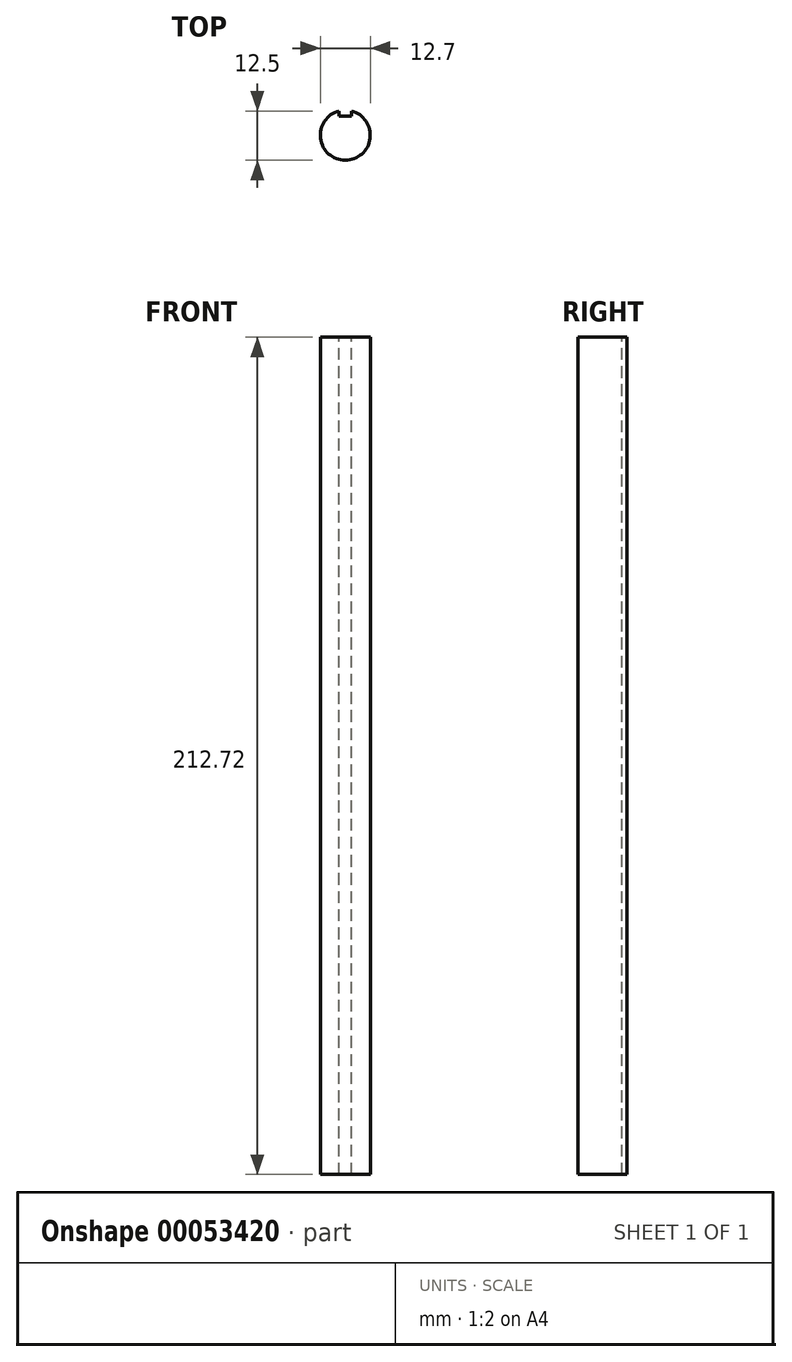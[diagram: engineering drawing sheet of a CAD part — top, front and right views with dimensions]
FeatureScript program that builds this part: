
annotation { "Feature Type Name" : "Feature", "Feature Type Description" : "" }
export const myFeature = defineFeature(function(context is Context, id is Id, definition is map)
    precondition{}
    {
        {
            var Q0;
            Q0=qCreatedBy(makeId("Top.planeOp"),FACE);
            var sketch = newSketch(context, id + "F0", { "sketchPlane" : qUnion([Q0])});
            skCircle(sketch, "E0", {"center": v(0, 0) * mm, "radius": 6.35 * mm});
            skSolve(sketch);
        }
        {
            var Q0;
            Q0=makeQuery(id+"F0.imprint","IMPRINT",FACE,{"disambiguationData":[TD([[makeQuery(id+"F0.imprint","IMPRINT",EDGE,{"derivedFrom":sQuery(id+"F0.wireOp",EDGE,"E0")}),1.0]])]});
            extrude(context, id + "F1", {"entities" : qUnion([Q0]), "depth" : 212.72 * mm});
        }
        {
            var Q0;
            Q0=makeQuery(id+"F1.opExtrude","CAP_FACE",FACE,{"disambiguationData":[OSD([sQuery(id+"F0.wireOp",EDGE,"E0")])],"isStart":false});
            var sketch = newSketch(context, id + "F2", { "sketchPlane" : qUnion([Q0])});
            skLineSegment(sketch, "E1.rect.bottom", {"start": v(1.59, 4.8) * mm, "end": v(-1.59, 4.8) * mm});
            skLineSegment(sketch, "E1.rect.top", {"start": v(1.59, 6.39) * mm, "end": v(-1.59, 6.39) * mm});
            skLineSegment(sketch, "E1.rect.left", {"start": v(1.59, 4.8) * mm, "end": v(1.59, 6.39) * mm});
            skLineSegment(sketch, "E1.rect.right", {"start": v(-1.59, 4.8) * mm, "end": v(-1.59, 6.39) * mm});
            skPoint(sketch, "E1.rect.middle", {"position": v(0, 5.6) * mm});
            skSolve(sketch);
        }
        {
            var Q0;
            {var subQ0=sQuery(id+"F2.wireOp",EDGE,"E1.rect.bottom");Q0=makeQuery(id+"F2.imprint","IMPRINT",FACE,{"disambiguationData":[TD([[makeQuery(id+"F2.imprint","IMPRINT",EDGE,{"derivedFrom":subQ0}),-1.0]])]});}
            extrude(context, id + "F3", {"entities" : qUnion([Q0]), "operationType" : NewBodyOperationType.REMOVE, "endBound" : BoundingType.THROUGH_ALL, "oppositeDirection" : true, "depth" : 25.4 * mm});
        }
    });
